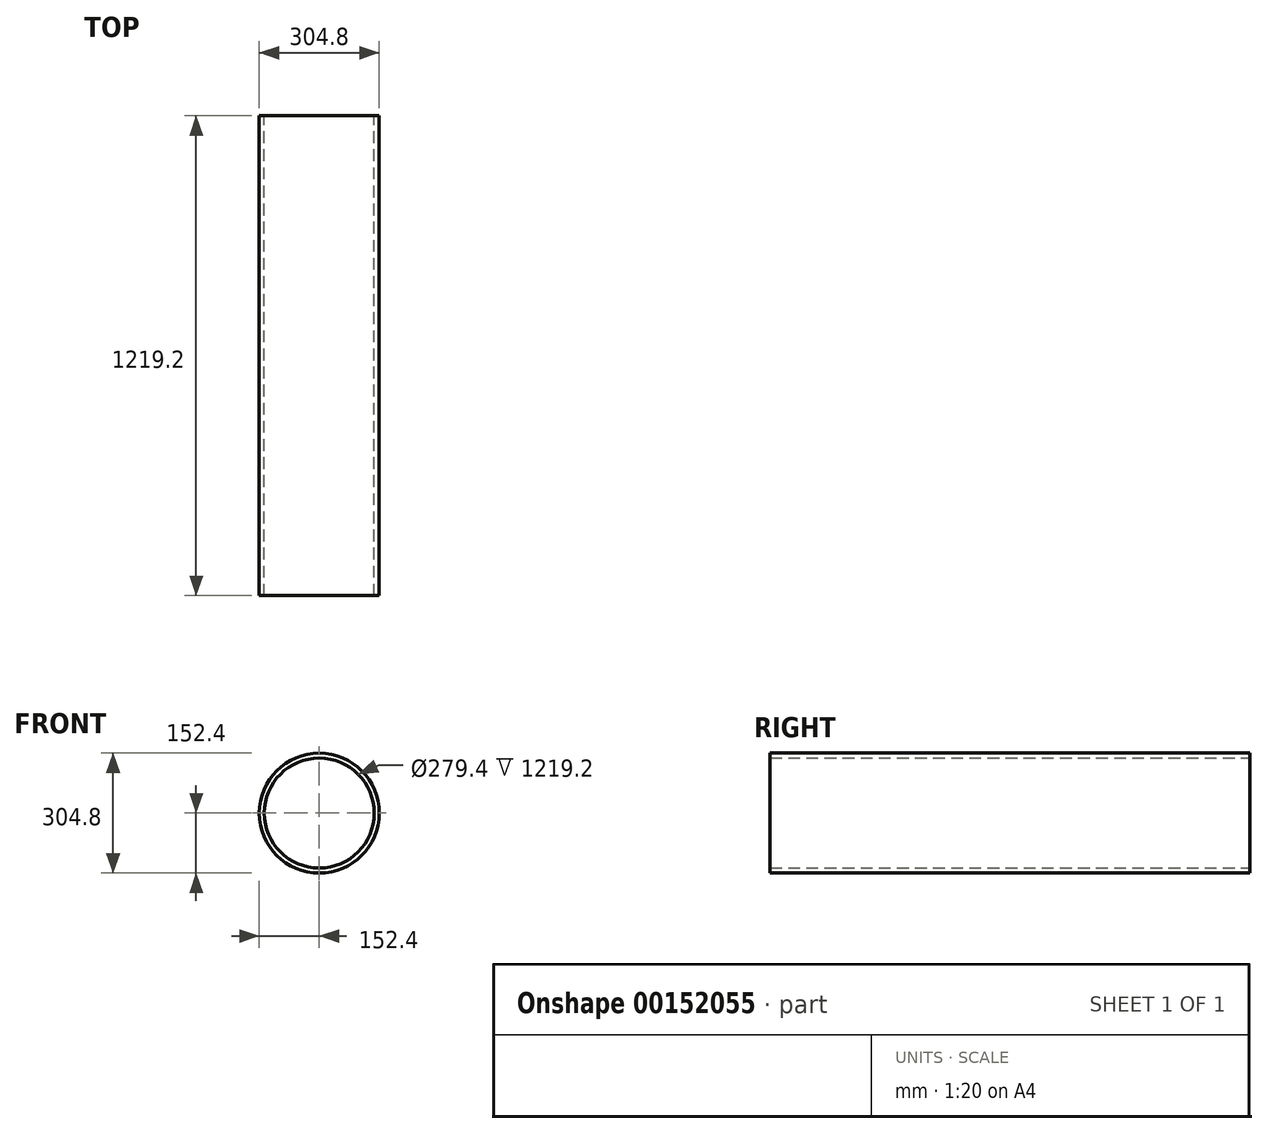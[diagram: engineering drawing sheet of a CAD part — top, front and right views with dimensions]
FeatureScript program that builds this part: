
annotation { "Feature Type Name" : "Feature", "Feature Type Description" : "" }
export const myFeature = defineFeature(function(context is Context, id is Id, definition is map)
    precondition{}
    {
        {
            var Q0;
            Q0=qCreatedBy(makeId("Front.planeOp"),FACE);
            var sketch = newSketch(context, id + "F0", { "sketchPlane" : qUnion([Q0])});
            skCircle(sketch, "E0", {"center": v(0, 0) * mm, "radius": 152.4 * mm});
            skCircle(sketch, "E1", {"center": v(0, 0) * mm, "radius": 139.7 * mm});
            skSolve(sketch);
        }
        {
            var Q0;
            Q0 = qSketchRegion(id + "F0", true);
            extrude(context, id + "F1", {"entities" : qUnion([Q0]), "depth" : 1219.2 * mm});
        }
    });
